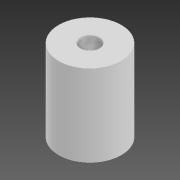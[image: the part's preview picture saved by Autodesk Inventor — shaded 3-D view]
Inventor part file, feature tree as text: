
AUTODESK INVENTOR PART (.ipt)
format: ipt  version: 2020 (Build 240168000, 168)  size: 80,384 bytes
history: native  units: in
note: dims shown in document units (in); Inventor stores cm internally (conversion verified against a paired STEP export)
features: extrude x1, sketch x1
ambient origin geometry x8: Origin, YZ Plane, XZ Plane, XY Plane, X Axis, Y Axis, Z Axis, Center Point
bodies: Solid1 (feature_tree)
feature tree (2):
  extrude  "Extrusion1"  Depth=0.5118in
  sketch  "Sketch1"  dims[d0=0.3937in d1=0.1181in d2=0.5118in d3=0.0in]
